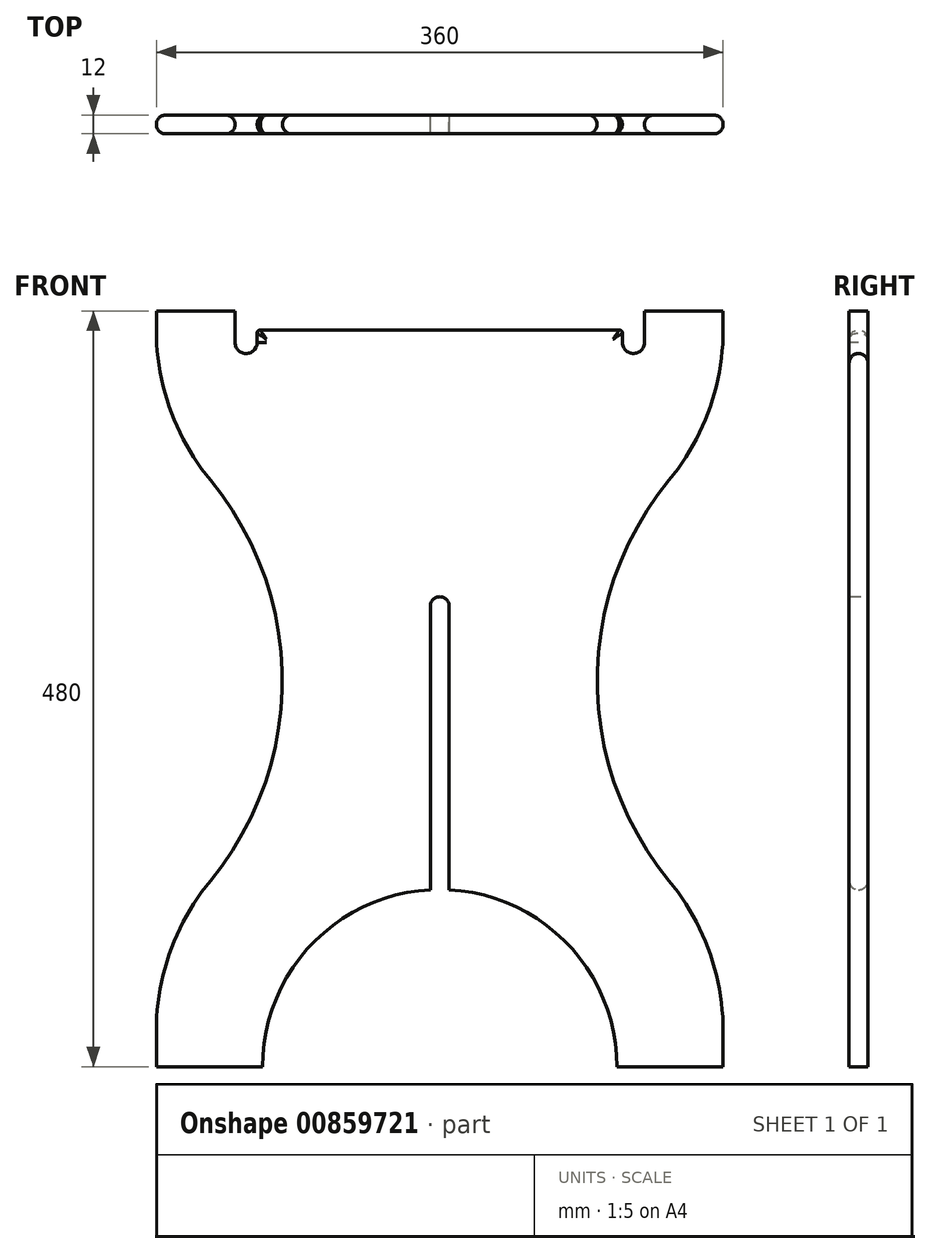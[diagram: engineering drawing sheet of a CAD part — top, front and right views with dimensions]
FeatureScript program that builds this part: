
annotation { "Feature Type Name" : "Feature", "Feature Type Description" : "" }
export const myFeature = defineFeature(function(context is Context, id is Id, definition is map)
    precondition{}
    {
        {
            var Q0;
            Q0=qCreatedBy(makeId("Front.planeOp"),FACE);
            var sketch = newSketch(context, id + "F0", { "sketchPlane" : qUnion([Q0])});
            skLineSegment(sketch, "E0.bottom", {"start": v(-180, -240) * mm, "end": v(-112.5, -240) * mm});
            skLineSegment(sketch, "E0.top", {"start": v(-180, 240) * mm, "end": v(-130, 240) * mm});
            skLineSegment(sketch, "E0.left", {"start": v(-180, -240) * mm, "end": v(-180, -217.42) * mm});
            skLineSegment(sketch, "E0.right", {"start": v(180, -240) * mm, "end": v(180, -217.42) * mm});
            skPoint(sketch, "E0.middle", {"position": v(0, 0) * mm});
            skLineSegment(sketch, "E1.0", {"start": v(-130, 228) * mm, "end": v(-130, 240) * mm});
            skLineSegment(sketch, "E2.0", {"start": v(130, 228) * mm, "end": v(130, 240) * mm});
            skLineSegment(sketch, "E3.trimOffspring", {"start": v(130, 240) * mm, "end": v(180, 240) * mm});
            skArc(sketch, "E4", {"start": v(112.5, -240) * mm, "mid": v(81.64, -162.6) * mm, "end": v(6, -127.66) * mm});
            skLineSegment(sketch, "E5.trimOffspring", {"start": v(112.5, -240) * mm, "end": v(180, -240) * mm});
            skArc(sketch, "E6", {"start": v(145.71, 132.55) * mm, "mid": v(100, 5.29) * mm, "end": v(145.71, -121.97) * mm});
            skArc(sketch, "E7", {"start": v(-145.71, -121.97) * mm, "mid": v(-100, 5.29) * mm, "end": v(-145.71, 132.55) * mm});
            skLineSegment(sketch, "E8.trimOffspring", {"start": v(-180, 228) * mm, "end": v(-180, 240) * mm});
            skLineSegment(sketch, "E9.trimOffspring", {"start": v(180, 228) * mm, "end": v(180, 240) * mm});
            skPoint(sketch, "E10.visualSharp", {"position": v(-180, 165.29) * mm});
            skArc(sketch, "E10.filletArc", {"start": v(-180, 228) * mm, "mid": v(-171.17, 177.3) * mm, "end": v(-145.71, 132.55) * mm});
            skPoint(sketch, "E11.visualSharp", {"position": v(-180, -154.71) * mm});
            skArc(sketch, "E11.filletArc", {"start": v(-145.71, -121.97) * mm, "mid": v(-171.17, -166.71) * mm, "end": v(-180, -217.42) * mm});
            skPoint(sketch, "E12.visualSharp", {"position": v(180, 165.29) * mm});
            skArc(sketch, "E12.filletArc", {"start": v(145.71, 132.55) * mm, "mid": v(171.17, 177.3) * mm, "end": v(180, 228) * mm});
            skPoint(sketch, "E13.visualSharp", {"position": v(180, -154.71) * mm});
            skArc(sketch, "E13.filletArc", {"start": v(180, -217.42) * mm, "mid": v(171.17, -166.71) * mm, "end": v(145.71, -121.97) * mm});
            skArc(sketch, "E14", {"start": v(116, 220) * mm, "mid": v(123, 213) * mm, "end": v(130, 220) * mm});
            skArc(sketch, "E15", {"start": v(-130, 220) * mm, "mid": v(-123, 213) * mm, "end": v(-116, 220) * mm});
            skLineSegment(sketch, "E16", {"start": v(-130, 228) * mm, "end": v(-130, 220) * mm});
            skLineSegment(sketch, "E17", {"start": v(-116, 220) * mm, "end": v(-116, 226) * mm});
            skLineSegment(sketch, "E18.trimOffspring", {"start": v(-114, 228) * mm, "end": v(114, 228) * mm});
            skLineSegment(sketch, "E19", {"start": v(130, 228) * mm, "end": v(130, 220) * mm});
            skLineSegment(sketch, "E20", {"start": v(116, 220) * mm, "end": v(116, 226) * mm});
            skPoint(sketch, "E21.visualSharp", {"position": v(-115.99, 228) * mm});
            skArc(sketch, "E21.filletArc", {"start": v(-114, 228) * mm, "mid": v(-115.4, 227.42) * mm, "end": v(-116, 226) * mm});
            skPoint(sketch, "E22.visualSharp", {"position": v(116, 228) * mm});
            skArc(sketch, "E22.filletArc", {"start": v(116, 226) * mm, "mid": v(115.41, 227.41) * mm, "end": v(114, 228) * mm});
            skLineSegment(sketch, "E23.0", {"start": v(6, -127.66) * mm, "end": v(6, 52.5) * mm});
            skLineSegment(sketch, "E24.0", {"start": v(-6, -127.66) * mm, "end": v(-6, 52.5) * mm});
            skArc(sketch, "E25", {"start": v(6, 52.5) * mm, "mid": v(0, 58.5) * mm, "end": v(-6, 52.5) * mm});
            skArc(sketch, "E26.trimOffspring", {"start": v(-6, -127.66) * mm, "mid": v(-81.64, -162.6) * mm, "end": v(-112.5, -240) * mm});
            skSolve(sketch);
        }
        {
            var Q0;
            Q0=makeQuery(id+"F0.imprint","IMPRINT",FACE,{"disambiguationData":[TD([[makeQuery(id+"F0.imprint","IMPRINT",EDGE,{"derivedFrom":sQuery(id+"F0.wireOp",EDGE,"E0.bottom")}),1.0]])]});
            extrude(context, id + "F1", {"entities" : qUnion([Q0]), "depth" : 12 * mm, "offsetDistance" : 25 * mm});
        }
        {
            var Q0;
            Q0=makeQuery(id+"F1.opExtrude","CAP_EDGE",EDGE,{"disambiguationData":[OSD([sQuery(id+"F0.wireOp",EDGE,"E9.trimOffspring")])],"isStart":false});
            var Q1;
            Q1=makeQuery(id+"F1.opExtrude","CAP_EDGE",EDGE,{"disambiguationData":[OSD([sQuery(id+"F0.wireOp",EDGE,"E12.filletArc")])],"isStart":true});
            var Q2;
            Q2=makeQuery(id+"F1.opExtrude","CAP_EDGE",EDGE,{"disambiguationData":[OSD([sQuery(id+"F0.wireOp",EDGE,"E11.filletArc")])],"isStart":false});
            var Q3;
            Q3=makeQuery(id+"F1.opExtrude","CAP_EDGE",EDGE,{"disambiguationData":[OSD([sQuery(id+"F0.wireOp",EDGE,"E7")])],"isStart":true});
            var Q4;
            Q4=makeQuery(id+"F1.opExtrude","CAP_EDGE",EDGE,{"disambiguationData":[OSD([sQuery(id+"F0.wireOp",EDGE,"E26.trimOffspring")])],"isStart":true});
            var Q5;
            Q5=makeQuery(id+"F1.opExtrude","CAP_EDGE",EDGE,{"disambiguationData":[OSD([sQuery(id+"F0.wireOp",EDGE,"E4")])],"isStart":true});
            var Q6;
            Q6=makeQuery(id+"F1.opExtrude","CAP_EDGE",EDGE,{"disambiguationData":[OSD([sQuery(id+"F0.wireOp",EDGE,"E26.trimOffspring")])],"isStart":false});
            var Q7;
            Q7=makeQuery(id+"F1.opExtrude","CAP_EDGE",EDGE,{"disambiguationData":[OSD([sQuery(id+"F0.wireOp",EDGE,"E4")])],"isStart":false});
            var Q8;
            Q8=makeQuery(id+"F1.opExtrude","CAP_EDGE",EDGE,{"disambiguationData":[OSD([sQuery(id+"F0.wireOp",EDGE,"E2.0"),sQuery(id+"F0.wireOp",EDGE,"E19")])],"isStart":false});
            var Q9;
            Q9=makeQuery(id+"F1.opExtrude","CAP_EDGE",EDGE,{"disambiguationData":[OSD([sQuery(id+"F0.wireOp",EDGE,"E1.0"),sQuery(id+"F0.wireOp",EDGE,"E16")])],"isStart":true});
            fillet(context, id + "F2", {"entities" : qUnion([Q0, Q1, Q2, Q3, Q4, Q5, Q6, Q7, Q8, Q9]), "radius" : 6 * mm, "tangentPropagation" : true, "allowEdgeOverflow" : false});
        }
    });
